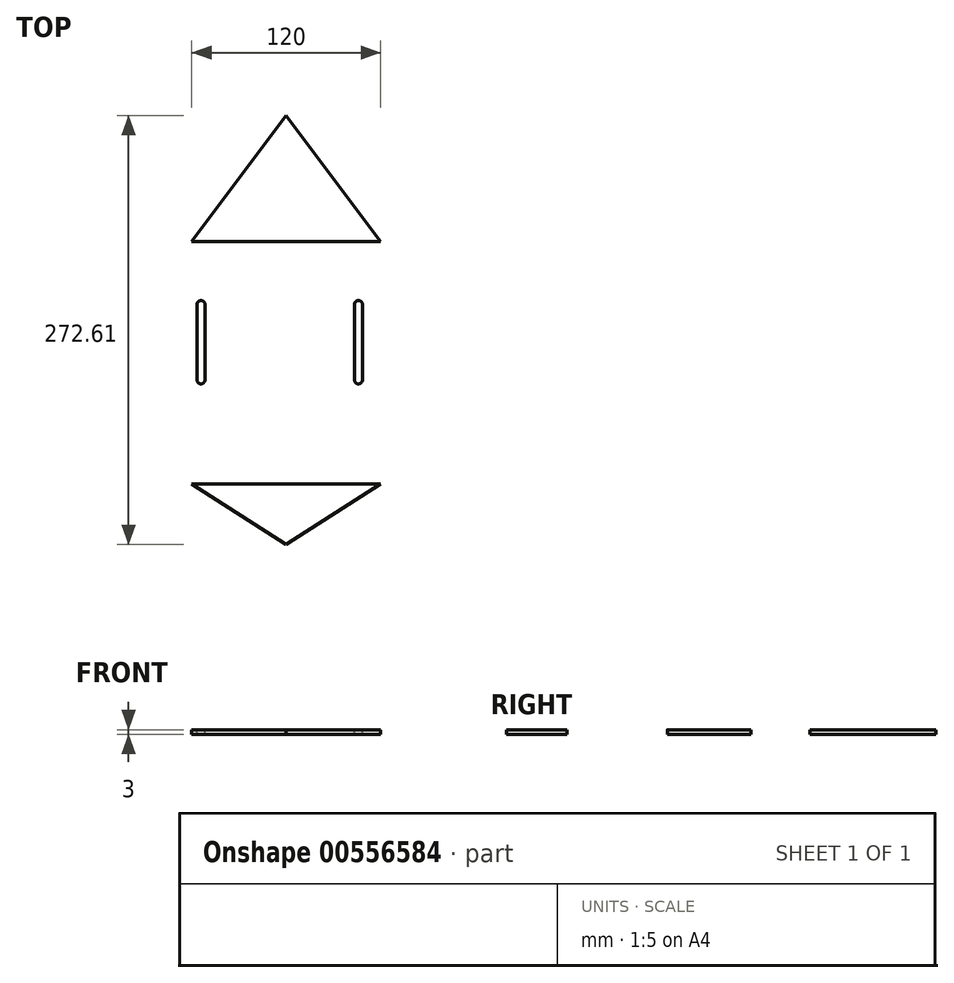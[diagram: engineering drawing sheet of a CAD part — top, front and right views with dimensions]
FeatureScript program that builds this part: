
annotation { "Feature Type Name" : "Feature", "Feature Type Description" : "" }
export const myFeature = defineFeature(function(context is Context, id is Id, definition is map)
    precondition{}
    {
        {
            var Q0;
            Q0=qCreatedBy(makeId("Top.planeOp"),FACE);
            var sketch = newSketch(context, id + "F0", { "sketchPlane" : qUnion([Q0])});
            skLineSegment(sketch, "E0", {"start": v(0, 32.93) * mm, "end": v(0, 0) * mm});
            skLineSegment(sketch, "E1", {"start": v(0, 0) * mm, "end": v(0, -107.07) * mm});
            skLineSegment(sketch, "E2", {"start": v(134.14, 0) * mm, "end": v(134.14, 32.93) * mm});
            skLineSegment(sketch, "E3", {"start": v(134.14, 32.93) * mm, "end": v(134.14, -107.07) * mm});
            skArc(sketch, "E4", {"start": v(0, -107.07) * mm, "mid": v(2.07, -112.07) * mm, "end": v(7.07, -114.14) * mm});
            skArc(sketch, "E5", {"start": v(0, 32.93) * mm, "mid": v(2.07, 37.93) * mm, "end": v(7.07, 40) * mm});
            skArc(sketch, "E6", {"start": v(134.14, -107.07) * mm, "mid": v(132.07, -112.07) * mm, "end": v(127.07, -114.14) * mm});
            skArc(sketch, "E7", {"start": v(134.14, 32.93) * mm, "mid": v(132.07, 37.93) * mm, "end": v(127.07, 40) * mm});
            skLineSegment(sketch, "E8", {"start": v(127.07, 40) * mm, "end": v(7.07, 40) * mm});
            skLineSegment(sketch, "E9", {"start": v(127.07, -114.14) * mm, "end": v(7.07, -114.14) * mm});
            skLineSegment(sketch, "E10", {"start": v(13, 0) * mm, "end": v(13, -48) * mm});
            skLineSegment(sketch, "E11", {"start": v(113, 0) * mm, "end": v(113, -48) * mm});
            skLineSegment(sketch, "E12", {"start": v(32, -9.03) * mm, "end": v(94, -9.03) * mm});
            skLineSegment(sketch, "E13", {"start": v(32, -39.53) * mm, "end": v(94, -39.53) * mm});
            skLineSegment(sketch, "E14", {"start": v(7.07, 40) * mm, "end": v(67.07, 120) * mm});
            skLineSegment(sketch, "E15", {"start": v(67.07, 120) * mm, "end": v(127.07, 40) * mm});
            skLineSegment(sketch, "E16", {"start": v(7.07, -114.14) * mm, "end": v(67.07, -152.61) * mm});
            skLineSegment(sketch, "E17", {"start": v(67.07, -152.61) * mm, "end": v(127.07, -114.14) * mm});
            skSolve(sketch);
        }
        {
            var Q0;
            Q0=makeQuery(id+"F0.imprint","IMPRINT",FACE,{"disambiguationData":[TD([[makeQuery(id+"F0.imprint","IMPRINT",EDGE,{"derivedFrom":sQuery(id+"F0.wireOp",EDGE,"E0")}),1.0]])]});
            extrude(context, id + "F1", {"entities" : qUnion([Q0]), "depth" : 3 * mm, "offsetDistance" : 25 * mm});
        }
        {
            var Q0;
            Q0=sQuery(id+"F0.wireOp",VERTEX,"E12.end");
            var Q1;
            Q1=sQuery(id+"F0.wireOp",VERTEX,"E12.start");
            var Q2;
            Q2=makeQuery(id+"F1.opExtrude","SWEPT_BODY",BODY,{"disambiguationData":[OSD([sQuery(id+"F0.wireOp",EDGE,"E0"),sQuery(id+"F0.wireOp",EDGE,"E1"),sQuery(id+"F0.wireOp",EDGE,"E3"),sQuery(id+"F0.wireOp",EDGE,"E4"),sQuery(id+"F0.wireOp",EDGE,"E5"),sQuery(id+"F0.wireOp",EDGE,"E6"),sQuery(id+"F0.wireOp",EDGE,"E7"),sQuery(id+"F0.wireOp",EDGE,"E8"),sQuery(id+"F0.wireOp",EDGE,"E9")])]});
            hole(context, id + "F2", {"style" : HoleStyle.SIMPLE, "endStyle" : HoleEndStyle.THROUGH, "oppositeDirection" : true, "holeDiameter" : 5 * mm, "isTappedThrough" : true, "tappedDepth" : 12 * mm, "tapClearance" : 3, "locations" : qUnion([Q0, Q1]), "scope" : qUnion([Q2])});
        }
        {
            var Q0;
            Q0=sQuery(id+"F0.wireOp",VERTEX,"E13.start");
            var Q1;
            Q1=sQuery(id+"F0.wireOp",VERTEX,"E13.end");
            var Q2;
            Q2=makeQuery(id+"F1.opExtrude","SWEPT_BODY",BODY,{"disambiguationData":[OSD([sQuery(id+"F0.wireOp",EDGE,"E0"),sQuery(id+"F0.wireOp",EDGE,"E1"),sQuery(id+"F0.wireOp",EDGE,"E3"),sQuery(id+"F0.wireOp",EDGE,"E4"),sQuery(id+"F0.wireOp",EDGE,"E5"),sQuery(id+"F0.wireOp",EDGE,"E6"),sQuery(id+"F0.wireOp",EDGE,"E7"),sQuery(id+"F0.wireOp",EDGE,"E8"),sQuery(id+"F0.wireOp",EDGE,"E9")])]});
            hole(context, id + "F3", {"style" : HoleStyle.SIMPLE, "endStyle" : HoleEndStyle.THROUGH, "oppositeDirection" : true, "holeDiameter" : 5 * mm, "isTappedThrough" : true, "tappedDepth" : 12 * mm, "tapClearance" : 3, "locations" : qUnion([Q0, Q1]), "scope" : qUnion([Q2])});
        }
        {
            var Q0;
            Q0=makeQuery(id+"F1.opExtrude","CAP_FACE",FACE,{"disambiguationData":[OSD([sQuery(id+"F0.wireOp",EDGE,"E0"),sQuery(id+"F0.wireOp",EDGE,"E1"),sQuery(id+"F0.wireOp",EDGE,"E3"),sQuery(id+"F0.wireOp",EDGE,"E4"),sQuery(id+"F0.wireOp",EDGE,"E5"),sQuery(id+"F0.wireOp",EDGE,"E6"),sQuery(id+"F0.wireOp",EDGE,"E7"),sQuery(id+"F0.wireOp",EDGE,"E8"),sQuery(id+"F0.wireOp",EDGE,"E9")])],"isStart":false});
            var sketch = newSketch(context, id + "F4", { "sketchPlane" : qUnion([Q0])});
            skLineSegment(sketch, "E18.JFt.JFt", {"start": v(113, 0) * mm, "end": v(113, -48) * mm, "construction": true});
            skArc(sketch, "E18.0.startCap", {"start": v(110.5, 0) * mm, "mid": v(113, 2.5) * mm, "end": v(115.5, 0) * mm});
            skArc(sketch, "E18.0.endCap", {"start": v(115.5, -48) * mm, "mid": v(113, -50.5) * mm, "end": v(110.5, -48) * mm});
            skLineSegment(sketch, "E18.0.left", {"start": v(115.5, 0) * mm, "end": v(115.5, -48) * mm});
            skLineSegment(sketch, "E18.0.right", {"start": v(110.5, 0) * mm, "end": v(110.5, -48) * mm});
            skLineSegment(sketch, "E19.JFp.JFp", {"start": v(13, 0) * mm, "end": v(13, -48) * mm, "construction": true});
            skArc(sketch, "E19.0.startCap", {"start": v(10.5, 0) * mm, "mid": v(13, 2.5) * mm, "end": v(15.5, 0) * mm});
            skArc(sketch, "E19.0.endCap", {"start": v(15.5, -48) * mm, "mid": v(13, -50.5) * mm, "end": v(10.5, -48) * mm});
            skLineSegment(sketch, "E19.0.left", {"start": v(15.5, 0) * mm, "end": v(15.5, -48) * mm});
            skLineSegment(sketch, "E19.0.right", {"start": v(10.5, 0) * mm, "end": v(10.5, -48) * mm});
            skSolve(sketch);
        }
        {
            var Q0;
            Q0=makeQuery(id+"F4.imprint","IMPRINT",FACE,{"disambiguationData":[TD([[makeQuery(id+"F4.imprint","IMPRINT",EDGE,{"derivedFrom":sQuery(id+"F4.wireOp",EDGE,"E18.0.startCap")}),-1.0]])]});
            extrude(context, id + "F5", {"entities" : qUnion([Q0]), "operationType" : NewBodyOperationType.REMOVE, "oppositeDirection" : true, "depth" : 25 * mm, "offsetDistance" : 25 * mm});
        }
        {
            var Q0;
            Q0=makeQuery(id+"F4.imprint","IMPRINT",FACE,{"disambiguationData":[TD([[makeQuery(id+"F4.imprint","IMPRINT",EDGE,{"derivedFrom":sQuery(id+"F4.wireOp",EDGE,"E19.0.startCap")}),-1.0]])]});
            extrude(context, id + "F6", {"entities" : qUnion([Q0]), "operationType" : NewBodyOperationType.REMOVE, "oppositeDirection" : true, "depth" : 25 * mm, "offsetDistance" : 25 * mm});
        }
        {
            var Q0;
            Q0=makeQuery(id+"F0.imprint","IMPRINT",FACE,{"disambiguationData":[TD([[makeQuery(id+"F0.imprint","IMPRINT",EDGE,{"derivedFrom":sQuery(id+"F0.wireOp",EDGE,"E8")}),-1.0]])]});
            var Q1;
            Q1=makeQuery(id+"F0.imprint","IMPRINT",FACE,{"disambiguationData":[TD([[makeQuery(id+"F0.imprint","IMPRINT",EDGE,{"derivedFrom":sQuery(id+"F0.wireOp",EDGE,"E9")}),1.0]])]});
            extrude(context, id + "F7", {"entities" : qUnion([Q0, Q1]), "operationType" : NewBodyOperationType.ADD, "depth" : 3 * mm, "offsetDistance" : 25 * mm});
        }
    });
